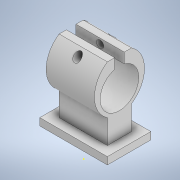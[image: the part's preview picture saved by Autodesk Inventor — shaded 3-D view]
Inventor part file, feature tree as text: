
AUTODESK INVENTOR PART (.ipt)
format: ipt  version: 2021 (Build 250183000, 183)  size: 195,072 bytes
history: native  units: in
note: dims shown in document units (in); Inventor stores cm internally (conversion verified against a paired STEP export)
features: sketch x7, extrude x4, hole x2
ambient origin geometry x8: Origin, YZ Plane, XZ Plane, XY Plane, X Axis, Y Axis, Z Axis, Center Point
bodies: Solid1 (feature_tree)
feature tree (13):
  extrude  "Extrusion1"  Depth=0.3937in
  extrude  "Extrusion4"  Depth=0.1969in
  extrude  "Extrusion5"  Depth=0.3937in
  hole  "Hole1"  [1 undecoded]
  extrude  "Extrusion6"  Depth=0.3937in
  sketch  "Sketch11"  dims[d31=0.1575in d33=0.1969in]
  hole  "Hole2"  [1 undecoded]
  sketch  "Sketch1"  dims[d0=0.1969in d1=0.3937in]
  sketch  "Sketch7"  dims[d2=0.1969in d3=0.1969in]
  sketch  "Sketch8"  dims[d4=0.3937in d5=0.2362in]
  sketch  "Sketch9"  dims[d6=0.2362in d10=0.3937in d11=0.0in]
  sketch  "Sketch10"  dims[d29=0.0984in d30=0.3937in]
  sketch  "Sketch12"  dims[d34=0.3937in d35=0.0in d36=0.0591in d37=0.0591in d39=0.0591in d40=0.3937in d41=0.0in d42=0.0315in d43=0.0419in d44=0.0837in d45=0.3937in d46=0.1969in d47=0.0591in d48=0.2362in d49=0.119in d50=0.0787in d51=0.5635in d52=0.315in d53=0.8108in d54=0.5512in d56=0.0787in d57=0.0787in d58=0.1969in d59=0.0984in d60=0.0787in d61=0.0591in d62=0.0in d63=0.2756in d64=0.1772in d65=0.3543in d66=0.1969in d67=0.1969in d68=0.2362in d69=0.119in d70=0.0787in d71=0.5635in d72=0.0591in d73=0.0in]
note: 2 required parameter values undecoded (feature->parameter linkage not recoverable at this tier; creation-order binding heuristic only, values carry confidence <= 0.55)
